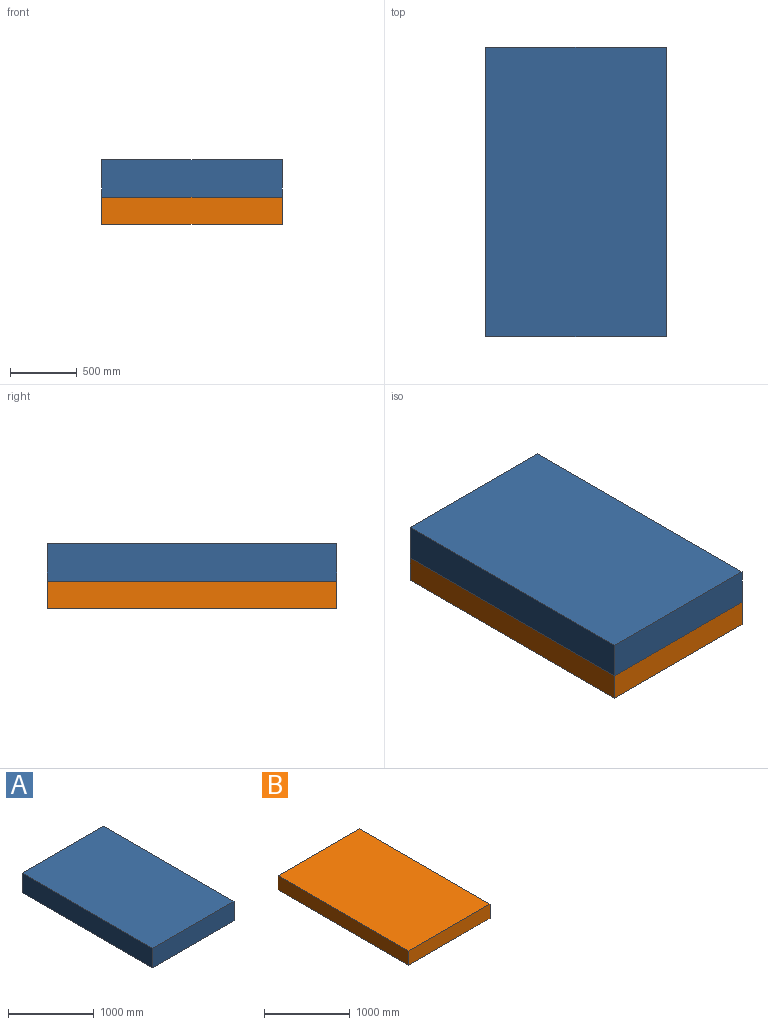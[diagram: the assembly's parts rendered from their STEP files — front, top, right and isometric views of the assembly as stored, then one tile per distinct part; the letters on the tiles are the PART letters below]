
ASSEMBLY  parts=2 mates=1
PART A: 6 faces, bbox 1346.2x2159x279.4 mm
  f0: plane 1346.2x279.4mm, normal (0,1,0), area 376128.3mm2, adj f1,f3,f4,f5
  f1: plane 2159x279.4mm, normal (-1,0,0), area 603224.6mm2, adj f0,f2,f4,f5
  f2: plane 1346.2x279.4mm, normal (0,-1,0), area 376128.3mm2, adj f1,f3,f4,f5
  f3: plane 2159x279.4mm, normal (1,0,0), area 603224.6mm2, adj f0,f2,f4,f5
  f4: plane 2159x1346.2mm, normal (0,0,1), area 2906445.8mm2, adj f0,f1,f2,f3
  f5: plane 2159x1346.2mm, normal (0,0,-1), area 2906445.8mm2, adj f0,f1,f2,f3
PART B: 6 faces, bbox 1346.2x2159x203.2 mm
  f0: plane 1346.2x203.2mm, normal (0,1,0), area 273547.8mm2, adj f1,f3,f4,f5
  f1: plane 2159x203.2mm, normal (-1,0,0), area 438708.8mm2, adj f0,f2,f4,f5
  f2: plane 1346.2x203.2mm, normal (0,-1,0), area 273547.8mm2, adj f1,f3,f4,f5
  f3: plane 2159x203.2mm, normal (1,0,0), area 438708.8mm2, adj f0,f2,f4,f5
  f4: plane 2159x1346.2mm, normal (0,0,1), area 2906445.8mm2, adj f0,f1,f2,f3
  f5: plane 2159x1346.2mm, normal (0,0,-1), area 2906445.8mm2, adj f0,f1,f2,f3
PLACE A t=(-27.78,274.36,462.37)mm
PLACE B t=(-27.78,274.36,259.17)mm fixed
MATE fastened B.f4 <-> A.f5  axis (0,0,1) through (-25.19,265.42,462.37)mm
